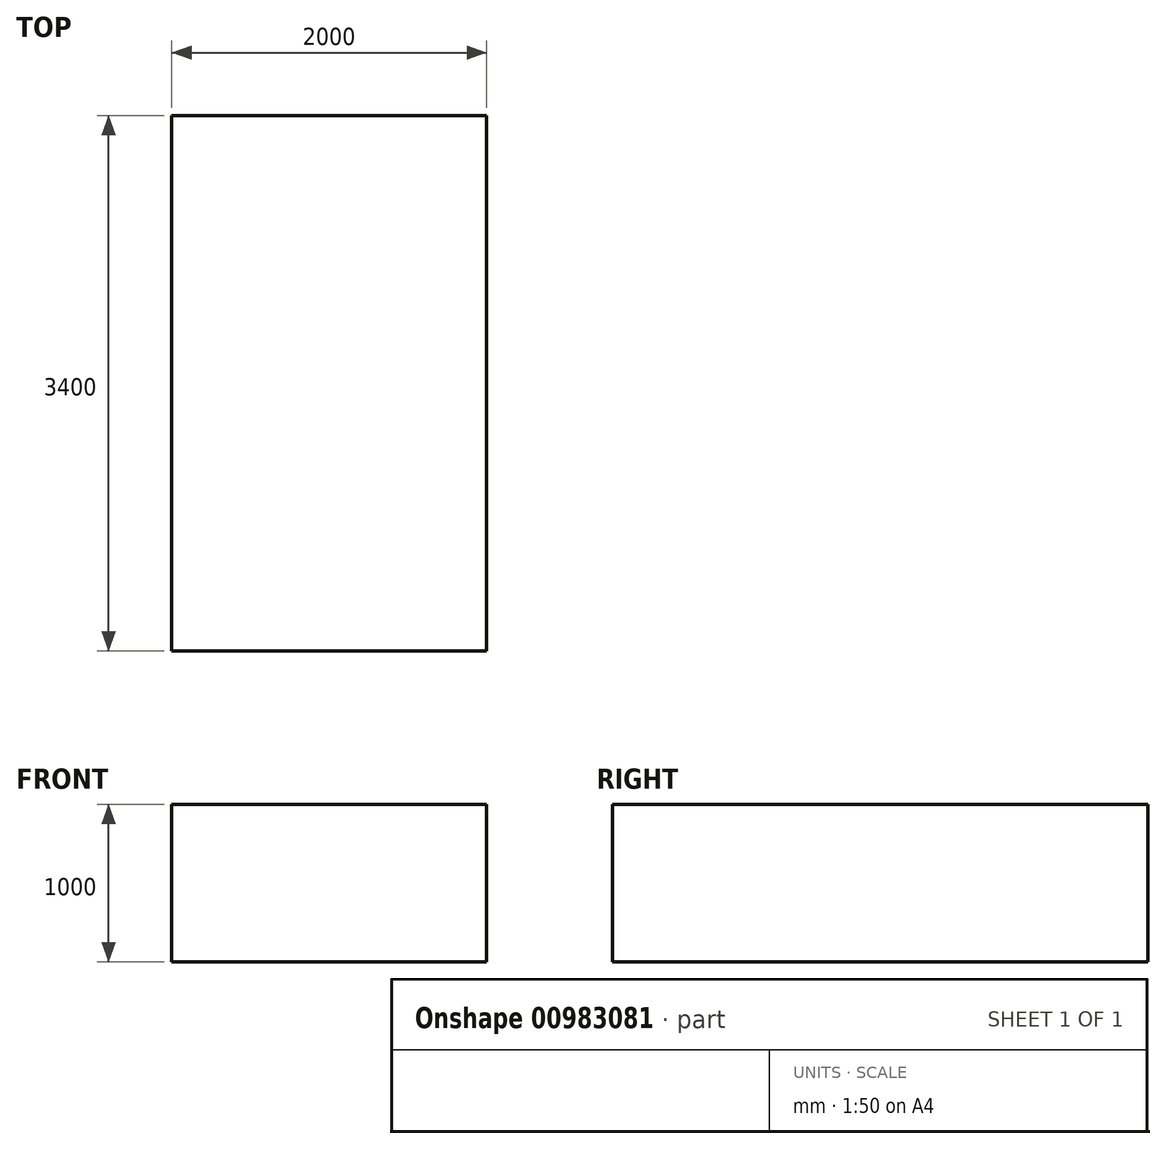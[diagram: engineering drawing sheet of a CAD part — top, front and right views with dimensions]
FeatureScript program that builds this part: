
annotation { "Feature Type Name" : "Feature", "Feature Type Description" : "" }
export const myFeature = defineFeature(function(context is Context, id is Id, definition is map)
    precondition{}
    {
        {
            var Q0;
            Q0=qCreatedBy(makeId("Top.planeOp"),FACE);
            var sketch = newSketch(context, id + "F0", { "sketchPlane" : qUnion([Q0])});
            skLineSegment(sketch, "E0.bottom", {"start": v(-1000, 1700) * mm, "end": v(1000, 1700) * mm});
            skLineSegment(sketch, "E0.top", {"start": v(-1000, -1700) * mm, "end": v(1000, -1700) * mm});
            skLineSegment(sketch, "E0.left", {"start": v(-1000, 1700) * mm, "end": v(-1000, -1700) * mm});
            skLineSegment(sketch, "E0.right", {"start": v(1000, 1700) * mm, "end": v(1000, -1700) * mm});
            skPoint(sketch, "E0.middle", {"position": v(0, 0) * mm});
            skSolve(sketch);
        }
        {
            var Q0;
            Q0 = qSketchRegion(id + "F0", true);
            extrude(context, id + "F1", {"entities" : qUnion([Q0]), "depth" : 1000 * mm, "offsetDistance" : 25 * mm});
        }
    });
